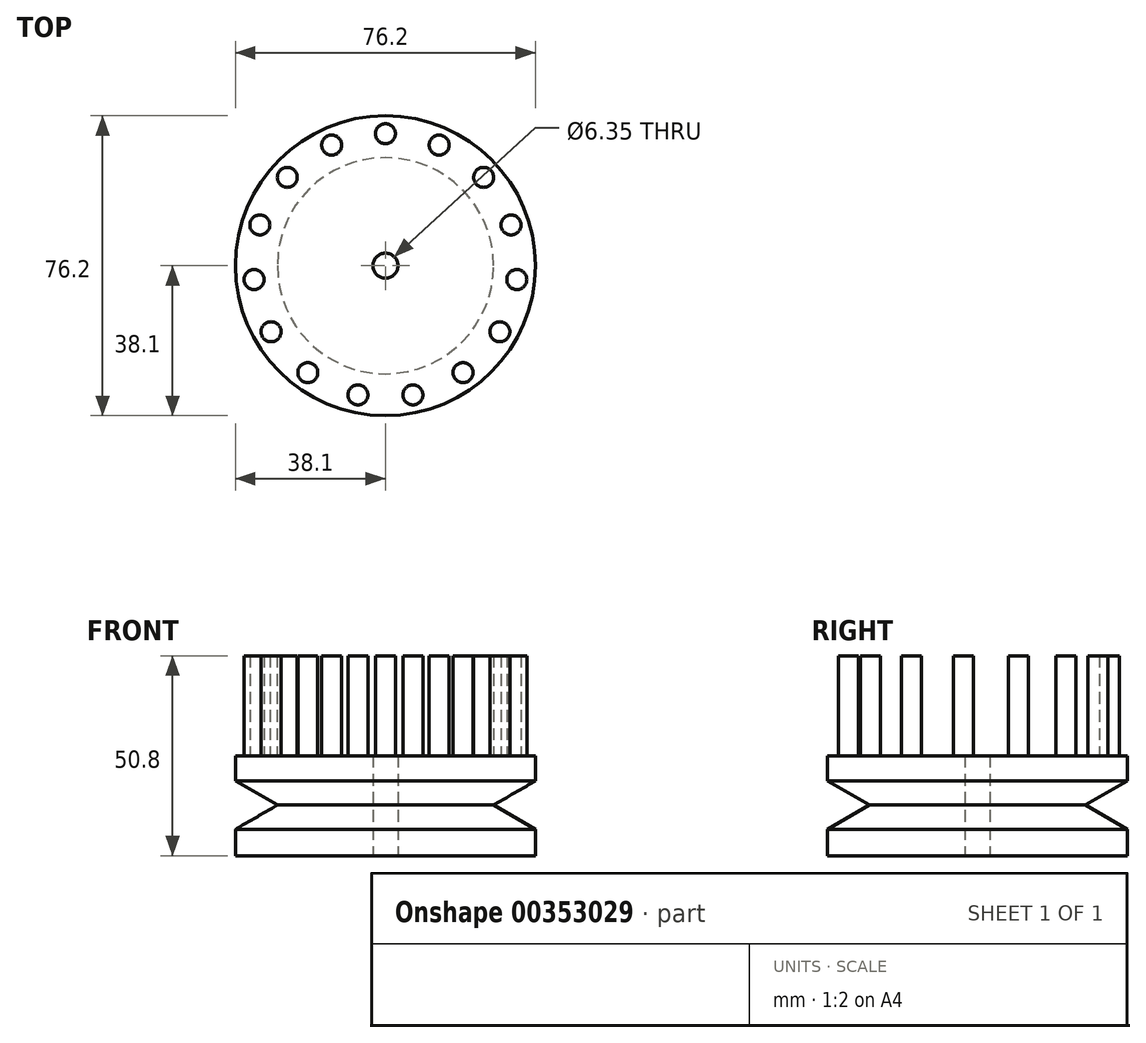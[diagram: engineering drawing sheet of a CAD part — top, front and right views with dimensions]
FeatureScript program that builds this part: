
annotation { "Feature Type Name" : "Feature", "Feature Type Description" : "" }
export const myFeature = defineFeature(function(context is Context, id is Id, definition is map)
    precondition{}
    {
        {
            var Q0;
            Q0=qCreatedBy(makeId("Top.planeOp"),FACE);
            var sketch = newSketch(context, id + "F0", { "sketchPlane" : qUnion([Q0])});
            skCircle(sketch, "E0", {"center": v(0, 0) * mm, "radius": 38.1 * mm});
            skCircle(sketch, "E1", {"center": v(0, 0) * mm, "radius": 3.18 * mm});
            skSolve(sketch);
        }
        {
            var Q0;
            Q0 = qSketchRegion(id + "F0", true);
            extrude(context, id + "F1", {"entities" : qUnion([Q0]), "depth" : 25.4 * mm});
        }
        {
            var Q0;
            Q0=makeQuery(id+"F1.opExtrude","CAP_FACE",FACE,{"disambiguationData":[OSD([sQuery(id+"F0.wireOp",EDGE,"E0"),sQuery(id+"F0.wireOp",EDGE,"E1")])],"isStart":false});
            var sketch = newSketch(context, id + "F2", { "sketchPlane" : qUnion([Q0])});
            skCircle(sketch, "E2", {"center": v(13.65, 30.65) * mm, "radius": 2.54 * mm});
            skCircle(sketch, "E3.1.0", {"center": v(0, 33.55) * mm, "radius": 2.54 * mm});
            skCircle(sketch, "E3.2.0", {"center": v(-13.65, 30.65) * mm, "radius": 2.54 * mm});
            skCircle(sketch, "E3.3.0", {"center": v(-24.93, 22.45) * mm, "radius": 2.54 * mm});
            skCircle(sketch, "E3.4.0", {"center": v(-31.91, 10.37) * mm, "radius": 2.54 * mm});
            skCircle(sketch, "E3.5.0", {"center": v(-33.37, -3.5) * mm, "radius": 2.54 * mm});
            skCircle(sketch, "E3.6.0", {"center": v(-29.06, -16.78) * mm, "radius": 2.54 * mm});
            skCircle(sketch, "E3.7.0", {"center": v(-19.72, -27.14) * mm, "radius": 2.54 * mm});
            skCircle(sketch, "E3.8.0", {"center": v(-6.98, -32.82) * mm, "radius": 2.54 * mm});
            skCircle(sketch, "E3.9.0", {"center": v(6.98, -32.82) * mm, "radius": 2.54 * mm});
            skCircle(sketch, "E3.10.0", {"center": v(19.72, -27.14) * mm, "radius": 2.54 * mm});
            skCircle(sketch, "E3.11.0", {"center": v(29.06, -16.78) * mm, "radius": 2.54 * mm});
            skCircle(sketch, "E3.12.0", {"center": v(33.37, -3.5) * mm, "radius": 2.54 * mm});
            skCircle(sketch, "E3.13.0", {"center": v(31.91, 10.37) * mm, "radius": 2.54 * mm});
            skCircle(sketch, "E3.14.0", {"center": v(24.93, 22.45) * mm, "radius": 2.54 * mm});
            skPoint(sketch, "E3.center", {"position": v(0, 0) * mm});
            skSolve(sketch);
        }
        {
            var Q0;
            Q0 = qSketchRegion(id + "F2", true);
            extrude(context, id + "F3", {"entities" : qUnion([Q0]), "operationType" : NewBodyOperationType.ADD, "depth" : 25.4 * mm});
        }
        {
            var Q0;
            Q0=qCreatedBy(makeId("Right.planeOp"),FACE);
            var sketch = newSketch(context, id + "F4", { "sketchPlane" : qUnion([Q0])});
            skLineSegment(sketch, "E4", {"start": v(0, 43.16) * mm, "end": v(0, -33.7) * mm});
            skSolve(sketch);
        }
        {
            var Q0;
            Q0=qCreatedBy(makeId("Right.planeOp"),FACE);
            var sketch = newSketch(context, id + "F5", { "sketchPlane" : qUnion([Q0])});
            skLineSegment(sketch, "E5", {"start": v(-38.46, 19.21) * mm, "end": v(-38.46, 6.51) * mm});
            skLineSegment(sketch, "E6", {"start": v(-38.46, 6.51) * mm, "end": v(-27.46, 12.86) * mm});
            skLineSegment(sketch, "E7", {"start": v(-27.46, 12.86) * mm, "end": v(-38.46, 19.21) * mm});
            skSolve(sketch);
        }
        {
            var Q0;
            Q0 = qSketchRegion(id + "F5", true);
            var Q1;
            Q1=sQuery(id+"F4.wireOp",EDGE,"E4");
            revolve(context, id + "F6", {"operationType" : NewBodyOperationType.REMOVE, "entities" : qUnion([Q0]), "axis" : qUnion([Q1]), "revolveType" : RevolveType.FULL});
        }
    });
